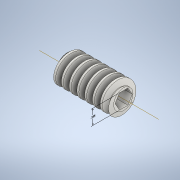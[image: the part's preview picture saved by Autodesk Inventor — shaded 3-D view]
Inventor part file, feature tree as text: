
AUTODESK INVENTOR PART (.ipt)
format: ipt  version: 2022.2 (Build 262287010, 287A)  size: 426,496 bytes
history: native  units: mm (DEFAULTED — no unit token found)
features: other x8, extrude x2, chamfer x2, pattern_circular x2, sketch x2, thicken_offset x1
ambient origin geometry x6: Origin, XZ Plane, X Axis, Y Axis, Z Axis, Center Point
bodies: Solid1 (feature_tree)
feature tree (17):
  other  "Annotations"
  extrude  "Base Body"  Depth=19.404171mm
  chamfer  "Chamfer1"  [1 undecoded]
  chamfer  "Chamfer2"  Distance=1.294799mm
  other  "Tooth Sketch"
  other  "Left Tooth"
  pattern_circular  "Left Tooth Pattern"  [2 undecoded]
  other  "Tooth"
  pattern_circular  "Tooth Pattern"  [2 undecoded]
  extrude  "Extrusion2"  Depth=9.779mm
  thicken_offset  "Thicken1"
  other  "Base Body Sketch"
  sketch  "Sketch5"  dims[d4=40.0mm d5=19.404171mm]
  other  "Srf1"
  sketch  "Sketch6"  dims[d6=38.1mm d7=0.0mm d8=1.294799mm d9=3.557431mm d10=1.294799mm d11=3.557431mm d12=19.198622mm d14=3.1425mm d24=19.198622mm d25=22.86mm d26=1.27mm d27=6.144654mm d28=8.085071mm d29=9.799106mm d30=5.08mm d31=10.0mm d32=100.0mm d33=0.0mm d34=90.0deg d35=90.0deg d36=0.0mm d37=0.0mm d43=10.0mm d45=360.0deg d46=45.0deg d47=45.0deg d49=0.0mm d53=0.0mm d54=56.595498mm d55=0.0mm d56=0.0mm d57=16.170142mm d58=25.4mm d59=0.0mm d60=5.08mm d61=25.4mm d62=100.0mm d63=0.0mm d64=90.0deg d65=90.0deg d66=0.0mm d67=0.0mm d68=10.0mm d69=10.0mm d70=360.0deg d72=10.0mm d74=10.0mm d75=10.0mm d76=0.0mm d77=56.595498mm d78=9.525mm d79=0.0mm d80=0.0mm d81=0.127mm d82=0.127mm d83=2.865495mm d84=9.779mm]
  other  "Pitch Diameter"
  other  "Linear Dimension 1"
note: 5 required parameter values undecoded (feature->parameter linkage not recoverable at this tier; creation-order binding heuristic only, values carry confidence <= 0.55)
